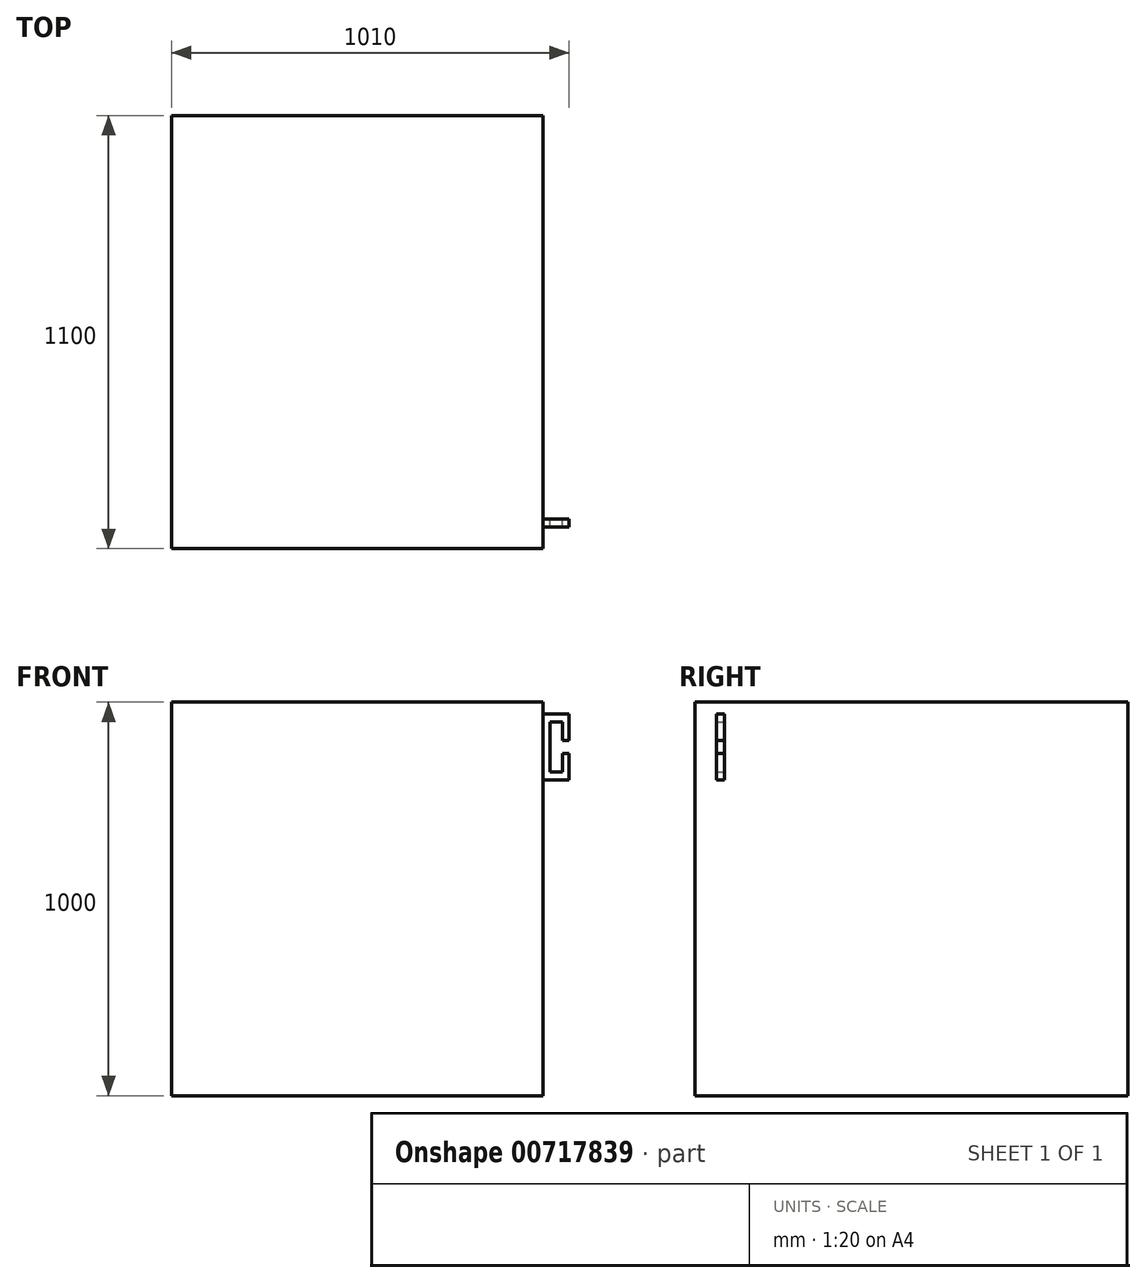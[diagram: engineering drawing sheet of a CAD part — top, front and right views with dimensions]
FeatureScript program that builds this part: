
annotation { "Feature Type Name" : "Feature", "Feature Type Description" : "" }
export const myFeature = defineFeature(function(context is Context, id is Id, definition is map)
    precondition{}
    {
        {
            var Q0;
            Q0=qCreatedBy(makeId("Front.planeOp"),FACE);
            var sketch = newSketch(context, id + "F0", { "sketchPlane" : qUnion([Q0])});
            skLineSegment(sketch, "E0.bottom", {"start": v(-472, 500) * mm, "end": v(472, 500) * mm});
            skLineSegment(sketch, "E0.top", {"start": v(-472, -500) * mm, "end": v(472, -500) * mm});
            skLineSegment(sketch, "E0.left", {"start": v(-472, 500) * mm, "end": v(-472, -500) * mm});
            skLineSegment(sketch, "E0.right", {"start": v(472, 500) * mm, "end": v(472, -500) * mm});
            skSolve(sketch);
        }
        {
            var Q0;
            Q0=makeQuery(id+"F0.imprint","IMPRINT",FACE,{"disambiguationData":[TD([[makeQuery(id+"F0.imprint","IMPRINT",EDGE,{"derivedFrom":sQuery(id+"F0.wireOp",EDGE,"E0.bottom")}),-1.0]])]});
            extrude(context, id + "F1", {"entities" : qUnion([Q0]), "endBound" : BoundingType.SYMMETRIC, "depth" : 1100 * mm, "offsetDistance" : 25 * mm});
        }
        {
            var Q0;
            Q0=qCreatedBy(makeId("Front.planeOp"),FACE);
            cPlane(context, id + "F2", {"entities" : qUnion([Q0]), "cplaneType" : CPlaneType.OFFSET, "offset" : (970 / 2) * mm, "width" : 150 * mm, "height" : 150 * mm});
        }
        {
            var Q0;
            Q0=qCreatedBy(id+"F2.planeOp",FACE);
            var sketch = newSketch(context, id + "F3", { "sketchPlane" : qUnion([Q0])});
            skLineSegment(sketch, "E1", {"start": v(0, 0) * mm, "end": v(472, 0) * mm, "construction": true});
            skLineSegment(sketch, "E2", {"start": v(472, 0) * mm, "end": v(472, 500) * mm, "construction": true});
            skLineSegment(sketch, "E3", {"start": v(550, 0) * mm, "end": v(472, 0) * mm, "construction": true});
            skLineSegment(sketch, "E4", {"start": v(472, 470) * mm, "end": v(538, 470) * mm});
            skLineSegment(sketch, "E5", {"start": v(538, 470) * mm, "end": v(538, 402) * mm});
            skLineSegment(sketch, "E6", {"start": v(538, 402) * mm, "end": v(521, 402) * mm});
            skLineSegment(sketch, "E7", {"start": v(521, 402) * mm, "end": v(521, 450) * mm});
            skLineSegment(sketch, "E8", {"start": v(521, 450) * mm, "end": v(489, 450) * mm});
            skLineSegment(sketch, "E9", {"start": v(489, 450) * mm, "end": v(489, 322) * mm});
            skLineSegment(sketch, "E10", {"start": v(489, 322) * mm, "end": v(521, 322) * mm});
            skLineSegment(sketch, "E11", {"start": v(521, 322) * mm, "end": v(521, 370) * mm});
            skLineSegment(sketch, "E12", {"start": v(521, 370) * mm, "end": v(538, 370) * mm});
            skLineSegment(sketch, "E13", {"start": v(538, 370) * mm, "end": v(538, 302) * mm});
            skLineSegment(sketch, "E14", {"start": v(538, 302) * mm, "end": v(472, 302) * mm});
            skLineSegment(sketch, "E15", {"start": v(472, 302) * mm, "end": v(472, 470) * mm});
            skLineSegment(sketch, "E16", {"start": v(489, 450) * mm, "end": v(472, 450) * mm, "construction": true});
            skLineSegment(sketch, "E17", {"start": v(489, 450) * mm, "end": v(489, 470) * mm, "construction": true});
            skLineSegment(sketch, "E18", {"start": v(489, 322) * mm, "end": v(489, 302) * mm, "construction": true});
            skSolve(sketch);
        }
        {
            var Q0;
            Q0=makeQuery(id+"F3.imprint","IMPRINT",FACE,{"disambiguationData":[TD([[makeQuery(id+"F3.imprint","IMPRINT",EDGE,{"derivedFrom":sQuery(id+"F3.wireOp",EDGE,"E4")}),-1.0]])]});
            extrude(context, id + "F4", {"entities" : qUnion([Q0]), "operationType" : NewBodyOperationType.ADD, "endBound" : BoundingType.SYMMETRIC, "depth" : 20 * mm, "offsetDistance" : 25 * mm});
        }
    });
